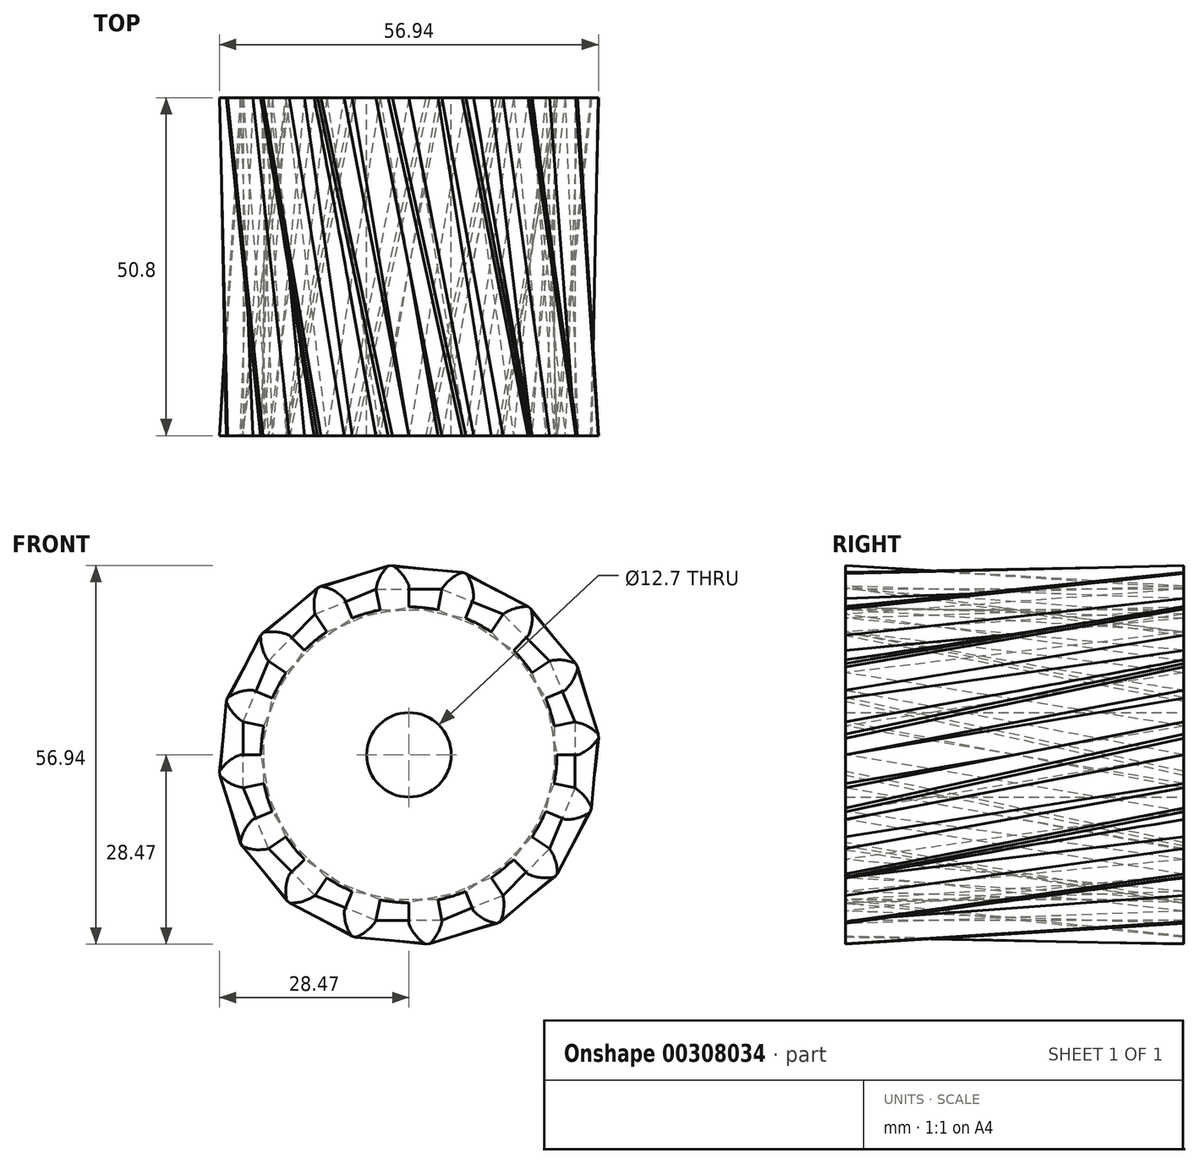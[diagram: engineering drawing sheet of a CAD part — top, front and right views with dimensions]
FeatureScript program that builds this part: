
annotation { "Feature Type Name" : "Feature", "Feature Type Description" : "" }
export const myFeature = defineFeature(function(context is Context, id is Id, definition is map)
    precondition{}
    {
        {
            var Q0;
            Q0=qCreatedBy(makeId("Front.planeOp"),FACE);
            var sketch = newSketch(context, id + "F0", { "sketchPlane" : qUnion([Q0])});
            skArc(sketch, "E0", {"start": v(-4.34, 21.8) * mm, "mid": v(-6.45, 21.27) * mm, "end": v(-8.5, 20.53) * mm});
            skArc(sketch, "E1.trimOffspring", {"start": v(0, 25.4) * mm, "mid": v(-1, 27.13) * mm, "end": v(-2.5, 28.47) * mm});
            skLineSegment(sketch, "E2", {"start": v(0, 25.4) * mm, "end": v(0, 22.23) * mm});
            skLineSegment(sketch, "E3", {"start": v(-2.5, 28.47) * mm, "end": v(-2.8, 28.44) * mm});
            skLineSegment(sketch, "E4.MirrorCS", {"start": v(-3.1, 28.4) * mm, "end": v(-2.8, 28.44) * mm});
            skArc(sketch, "E5.MirrorCS", {"start": v(-4.96, 24.91) * mm, "mid": v(-4.3, 26.8) * mm, "end": v(-3.1, 28.4) * mm});
            skLineSegment(sketch, "E6.MirrorCS", {"start": v(-4.96, 24.91) * mm, "end": v(-4.34, 21.8) * mm});
            skLineSegment(sketch, "E7.1.0", {"start": v(-14.11, 21.12) * mm, "end": v(-12.35, 18.48) * mm});
            skArc(sketch, "E7.1.1", {"start": v(-14.11, 21.12) * mm, "mid": v(-14.24, 23.12) * mm, "end": v(-13.74, 25.06) * mm});
            skLineSegment(sketch, "E7.1.2", {"start": v(-13.74, 25.06) * mm, "end": v(-13.47, 25.2) * mm});
            skLineSegment(sketch, "E7.1.3", {"start": v(-13.2, 25.34) * mm, "end": v(-13.47, 25.2) * mm});
            skArc(sketch, "E7.1.4", {"start": v(-9.72, 23.47) * mm, "mid": v(-11.31, 24.68) * mm, "end": v(-13.2, 25.34) * mm});
            skLineSegment(sketch, "E7.1.5", {"start": v(-9.72, 23.47) * mm, "end": v(-8.5, 20.53) * mm});
            skLineSegment(sketch, "E7.2.0", {"start": v(-21.12, 14.11) * mm, "end": v(-18.48, 12.35) * mm});
            skArc(sketch, "E7.2.1", {"start": v(-21.12, 14.11) * mm, "mid": v(-22, 15.9) * mm, "end": v(-22.28, 17.9) * mm});
            skLineSegment(sketch, "E7.2.2", {"start": v(-22.28, 17.9) * mm, "end": v(-22.09, 18.13) * mm});
            skLineSegment(sketch, "E7.2.3", {"start": v(-21.9, 18.36) * mm, "end": v(-22.09, 18.13) * mm});
            skArc(sketch, "E7.2.4", {"start": v(-17.96, 17.96) * mm, "mid": v(-19.9, 18.48) * mm, "end": v(-21.9, 18.36) * mm});
            skLineSegment(sketch, "E7.2.5", {"start": v(-17.96, 17.96) * mm, "end": v(-15.72, 15.72) * mm});
            skLineSegment(sketch, "E7.3.0", {"start": v(-24.91, 4.96) * mm, "end": v(-21.8, 4.34) * mm});
            skArc(sketch, "E7.3.1", {"start": v(-24.91, 4.96) * mm, "mid": v(-26.41, 6.28) * mm, "end": v(-27.43, 8) * mm});
            skLineSegment(sketch, "E7.3.2", {"start": v(-27.43, 8) * mm, "end": v(-27.34, 8.3) * mm});
            skLineSegment(sketch, "E7.3.3", {"start": v(-27.25, 8.59) * mm, "end": v(-27.34, 8.3) * mm});
            skArc(sketch, "E7.3.4", {"start": v(-23.47, 9.72) * mm, "mid": v(-25.45, 9.46) * mm, "end": v(-27.25, 8.59) * mm});
            skLineSegment(sketch, "E7.3.5", {"start": v(-23.47, 9.72) * mm, "end": v(-20.53, 8.5) * mm});
            skLineSegment(sketch, "E7.4.0", {"start": v(-24.91, -4.96) * mm, "end": v(-21.8, -4.34) * mm});
            skArc(sketch, "E7.4.1", {"start": v(-24.91, -4.96) * mm, "mid": v(-26.8, -4.3) * mm, "end": v(-28.4, -3.1) * mm});
            skLineSegment(sketch, "E7.4.2", {"start": v(-28.4, -3.1) * mm, "end": v(-28.44, -2.8) * mm});
            skLineSegment(sketch, "E7.4.3", {"start": v(-28.47, -2.5) * mm, "end": v(-28.44, -2.8) * mm});
            skArc(sketch, "E7.4.4", {"start": v(-25.4, 0) * mm, "mid": v(-27.13, -1) * mm, "end": v(-28.47, -2.5) * mm});
            skLineSegment(sketch, "E7.4.5", {"start": v(-25.4, 0) * mm, "end": v(-22.23, 0) * mm});
            skLineSegment(sketch, "E7.5.0", {"start": v(-21.12, -14.11) * mm, "end": v(-18.48, -12.35) * mm});
            skArc(sketch, "E7.5.1", {"start": v(-21.12, -14.11) * mm, "mid": v(-23.12, -14.24) * mm, "end": v(-25.06, -13.74) * mm});
            skLineSegment(sketch, "E7.5.2", {"start": v(-25.06, -13.74) * mm, "end": v(-25.2, -13.47) * mm});
            skLineSegment(sketch, "E7.5.3", {"start": v(-25.34, -13.2) * mm, "end": v(-25.2, -13.47) * mm});
            skArc(sketch, "E7.5.4", {"start": v(-23.47, -9.72) * mm, "mid": v(-24.68, -11.31) * mm, "end": v(-25.34, -13.2) * mm});
            skLineSegment(sketch, "E7.5.5", {"start": v(-23.47, -9.72) * mm, "end": v(-20.53, -8.5) * mm});
            skLineSegment(sketch, "E7.6.0", {"start": v(-14.11, -21.12) * mm, "end": v(-12.35, -18.48) * mm});
            skArc(sketch, "E7.6.1", {"start": v(-14.11, -21.12) * mm, "mid": v(-15.9, -22) * mm, "end": v(-17.9, -22.28) * mm});
            skLineSegment(sketch, "E7.6.2", {"start": v(-17.9, -22.28) * mm, "end": v(-18.13, -22.09) * mm});
            skLineSegment(sketch, "E7.6.3", {"start": v(-18.36, -21.9) * mm, "end": v(-18.13, -22.09) * mm});
            skArc(sketch, "E7.6.4", {"start": v(-17.96, -17.96) * mm, "mid": v(-18.48, -19.9) * mm, "end": v(-18.36, -21.9) * mm});
            skLineSegment(sketch, "E7.6.5", {"start": v(-17.96, -17.96) * mm, "end": v(-15.72, -15.72) * mm});
            skLineSegment(sketch, "E7.7.0", {"start": v(-4.96, -24.91) * mm, "end": v(-4.34, -21.8) * mm});
            skArc(sketch, "E7.7.1", {"start": v(-4.96, -24.91) * mm, "mid": v(-6.28, -26.41) * mm, "end": v(-8, -27.43) * mm});
            skLineSegment(sketch, "E7.7.2", {"start": v(-8, -27.43) * mm, "end": v(-8.3, -27.34) * mm});
            skLineSegment(sketch, "E7.7.3", {"start": v(-8.59, -27.25) * mm, "end": v(-8.3, -27.34) * mm});
            skArc(sketch, "E7.7.4", {"start": v(-9.72, -23.47) * mm, "mid": v(-9.46, -25.45) * mm, "end": v(-8.59, -27.25) * mm});
            skLineSegment(sketch, "E7.7.5", {"start": v(-9.72, -23.47) * mm, "end": v(-8.5, -20.53) * mm});
            skLineSegment(sketch, "E7.8.0", {"start": v(4.96, -24.91) * mm, "end": v(4.34, -21.8) * mm});
            skArc(sketch, "E7.8.1", {"start": v(4.96, -24.91) * mm, "mid": v(4.3, -26.8) * mm, "end": v(3.1, -28.4) * mm});
            skLineSegment(sketch, "E7.8.2", {"start": v(3.1, -28.4) * mm, "end": v(2.8, -28.44) * mm});
            skLineSegment(sketch, "E7.8.3", {"start": v(2.5, -28.47) * mm, "end": v(2.8, -28.44) * mm});
            skArc(sketch, "E7.8.4", {"start": v(0, -25.4) * mm, "mid": v(1, -27.13) * mm, "end": v(2.5, -28.47) * mm});
            skLineSegment(sketch, "E7.8.5", {"start": v(0, -25.4) * mm, "end": v(0, -22.23) * mm});
            skLineSegment(sketch, "E7.9.0", {"start": v(14.11, -21.12) * mm, "end": v(12.35, -18.48) * mm});
            skArc(sketch, "E7.9.1", {"start": v(14.11, -21.12) * mm, "mid": v(14.24, -23.12) * mm, "end": v(13.74, -25.06) * mm});
            skLineSegment(sketch, "E7.9.2", {"start": v(13.74, -25.06) * mm, "end": v(13.47, -25.2) * mm});
            skLineSegment(sketch, "E7.9.3", {"start": v(13.2, -25.34) * mm, "end": v(13.47, -25.2) * mm});
            skArc(sketch, "E7.9.4", {"start": v(9.72, -23.47) * mm, "mid": v(11.31, -24.68) * mm, "end": v(13.2, -25.34) * mm});
            skLineSegment(sketch, "E7.9.5", {"start": v(9.72, -23.47) * mm, "end": v(8.5, -20.53) * mm});
            skLineSegment(sketch, "E7.10.0", {"start": v(21.12, -14.11) * mm, "end": v(18.48, -12.35) * mm});
            skArc(sketch, "E7.10.1", {"start": v(21.12, -14.11) * mm, "mid": v(22, -15.9) * mm, "end": v(22.28, -17.9) * mm});
            skLineSegment(sketch, "E7.10.2", {"start": v(22.28, -17.9) * mm, "end": v(22.09, -18.13) * mm});
            skLineSegment(sketch, "E7.10.3", {"start": v(21.9, -18.36) * mm, "end": v(22.09, -18.13) * mm});
            skArc(sketch, "E7.10.4", {"start": v(17.96, -17.96) * mm, "mid": v(19.9, -18.48) * mm, "end": v(21.9, -18.36) * mm});
            skLineSegment(sketch, "E7.10.5", {"start": v(17.96, -17.96) * mm, "end": v(15.72, -15.72) * mm});
            skLineSegment(sketch, "E7.11.0", {"start": v(24.91, -4.96) * mm, "end": v(21.8, -4.34) * mm});
            skArc(sketch, "E7.11.1", {"start": v(24.91, -4.96) * mm, "mid": v(26.41, -6.28) * mm, "end": v(27.43, -8) * mm});
            skLineSegment(sketch, "E7.11.2", {"start": v(27.43, -8) * mm, "end": v(27.34, -8.3) * mm});
            skLineSegment(sketch, "E7.11.3", {"start": v(27.25, -8.59) * mm, "end": v(27.34, -8.3) * mm});
            skArc(sketch, "E7.11.4", {"start": v(23.47, -9.72) * mm, "mid": v(25.45, -9.46) * mm, "end": v(27.25, -8.59) * mm});
            skLineSegment(sketch, "E7.11.5", {"start": v(23.47, -9.72) * mm, "end": v(20.53, -8.5) * mm});
            skLineSegment(sketch, "E7.12.0", {"start": v(24.91, 4.96) * mm, "end": v(21.8, 4.34) * mm});
            skArc(sketch, "E7.12.1", {"start": v(24.91, 4.96) * mm, "mid": v(26.8, 4.3) * mm, "end": v(28.4, 3.1) * mm});
            skLineSegment(sketch, "E7.12.2", {"start": v(28.4, 3.1) * mm, "end": v(28.44, 2.8) * mm});
            skLineSegment(sketch, "E7.12.3", {"start": v(28.47, 2.5) * mm, "end": v(28.44, 2.8) * mm});
            skArc(sketch, "E7.12.4", {"start": v(25.4, 0) * mm, "mid": v(27.13, 1) * mm, "end": v(28.47, 2.5) * mm});
            skLineSegment(sketch, "E7.12.5", {"start": v(25.4, 0) * mm, "end": v(22.23, 0) * mm});
            skLineSegment(sketch, "E7.13.0", {"start": v(21.12, 14.11) * mm, "end": v(18.48, 12.35) * mm});
            skArc(sketch, "E7.13.1", {"start": v(21.12, 14.11) * mm, "mid": v(23.12, 14.24) * mm, "end": v(25.06, 13.74) * mm});
            skLineSegment(sketch, "E7.13.2", {"start": v(25.06, 13.74) * mm, "end": v(25.2, 13.47) * mm});
            skLineSegment(sketch, "E7.13.3", {"start": v(25.34, 13.2) * mm, "end": v(25.2, 13.47) * mm});
            skArc(sketch, "E7.13.4", {"start": v(23.47, 9.72) * mm, "mid": v(24.68, 11.31) * mm, "end": v(25.34, 13.2) * mm});
            skLineSegment(sketch, "E7.13.5", {"start": v(23.47, 9.72) * mm, "end": v(20.53, 8.5) * mm});
            skLineSegment(sketch, "E7.14.0", {"start": v(14.11, 21.12) * mm, "end": v(12.35, 18.48) * mm});
            skArc(sketch, "E7.14.1", {"start": v(14.11, 21.12) * mm, "mid": v(15.9, 22) * mm, "end": v(17.9, 22.28) * mm});
            skLineSegment(sketch, "E7.14.2", {"start": v(17.9, 22.28) * mm, "end": v(18.13, 22.09) * mm});
            skLineSegment(sketch, "E7.14.3", {"start": v(18.36, 21.9) * mm, "end": v(18.13, 22.09) * mm});
            skArc(sketch, "E7.14.4", {"start": v(17.96, 17.96) * mm, "mid": v(18.48, 19.9) * mm, "end": v(18.36, 21.9) * mm});
            skLineSegment(sketch, "E7.14.5", {"start": v(17.96, 17.96) * mm, "end": v(15.72, 15.72) * mm});
            skLineSegment(sketch, "E7.15.0", {"start": v(4.96, 24.91) * mm, "end": v(4.34, 21.8) * mm});
            skArc(sketch, "E7.15.1", {"start": v(4.96, 24.91) * mm, "mid": v(6.28, 26.41) * mm, "end": v(8, 27.43) * mm});
            skLineSegment(sketch, "E7.15.2", {"start": v(8, 27.43) * mm, "end": v(8.3, 27.34) * mm});
            skLineSegment(sketch, "E7.15.3", {"start": v(8.59, 27.25) * mm, "end": v(8.3, 27.34) * mm});
            skArc(sketch, "E7.15.4", {"start": v(9.72, 23.47) * mm, "mid": v(9.46, 25.45) * mm, "end": v(8.59, 27.25) * mm});
            skLineSegment(sketch, "E7.15.5", {"start": v(9.72, 23.47) * mm, "end": v(8.5, 20.53) * mm});
            skArc(sketch, "E8.trimOffspring", {"start": v(4.34, 21.8) * mm, "mid": v(2.18, 22.12) * mm, "end": v(0, 22.23) * mm});
            skArc(sketch, "E9.trimOffspring", {"start": v(-12.35, 18.48) * mm, "mid": v(-14.1, 17.18) * mm, "end": v(-15.72, 15.72) * mm});
            skArc(sketch, "E10.trimOffspring", {"start": v(12.35, 18.48) * mm, "mid": v(10.48, 19.6) * mm, "end": v(8.5, 20.53) * mm});
            skArc(sketch, "E11.trimOffspring", {"start": v(18.48, 12.35) * mm, "mid": v(17.18, 14.1) * mm, "end": v(15.72, 15.72) * mm});
            skArc(sketch, "E12.trimOffspring", {"start": v(21.8, 4.34) * mm, "mid": v(21.27, 6.45) * mm, "end": v(20.53, 8.5) * mm});
            skArc(sketch, "E13.trimOffspring", {"start": v(21.8, -4.34) * mm, "mid": v(22.12, -2.18) * mm, "end": v(22.23, 0) * mm});
            skArc(sketch, "E14.trimOffspring", {"start": v(18.48, -12.35) * mm, "mid": v(19.6, -10.48) * mm, "end": v(20.53, -8.5) * mm});
            skArc(sketch, "E15.trimOffspring", {"start": v(12.35, -18.48) * mm, "mid": v(14.1, -17.18) * mm, "end": v(15.72, -15.72) * mm});
            skArc(sketch, "E16.trimOffspring", {"start": v(4.34, -21.8) * mm, "mid": v(6.45, -21.27) * mm, "end": v(8.5, -20.53) * mm});
            skArc(sketch, "E17.trimOffspring", {"start": v(-4.34, -21.8) * mm, "mid": v(-2.18, -22.12) * mm, "end": v(0, -22.23) * mm});
            skArc(sketch, "E18.trimOffspring", {"start": v(-12.35, -18.48) * mm, "mid": v(-10.48, -19.6) * mm, "end": v(-8.5, -20.53) * mm});
            skArc(sketch, "E19.trimOffspring", {"start": v(-18.48, -12.35) * mm, "mid": v(-17.18, -14.1) * mm, "end": v(-15.72, -15.72) * mm});
            skArc(sketch, "E20.trimOffspring", {"start": v(-21.8, -4.34) * mm, "mid": v(-21.27, -6.45) * mm, "end": v(-20.53, -8.5) * mm});
            skArc(sketch, "E21.trimOffspring", {"start": v(-21.8, 4.34) * mm, "mid": v(-22.12, 2.18) * mm, "end": v(-22.23, 0) * mm});
            skArc(sketch, "E22.trimOffspring", {"start": v(-18.48, 12.35) * mm, "mid": v(-19.6, 10.48) * mm, "end": v(-20.53, 8.5) * mm});
            skSolve(sketch);
        }
        {
            var Q0;
            Q0=makeQuery(id+"F0.imprint","IMPRINT",FACE,{"disambiguationData":[TD([[makeQuery(id+"F0.imprint","IMPRINT",EDGE,{"derivedFrom":sQuery(id+"F0.wireOp",EDGE,"E0")}),1.0]])]});
            cPlane(context, id + "F1", {"entities" : qUnion([Q0]), "cplaneType" : CPlaneType.OFFSET, "offset" : 50.8 * mm, "width" : 152.4 * mm, "height" : 152.4 * mm});
        }
        {
            var Q0;
            Q0=qCreatedBy(id+"F1.planeOp",FACE);
            var sketch = newSketch(context, id + "F2", { "sketchPlane" : qUnion([Q0])});
            skArc(sketch, "E23.0.0", {"start": v(-27.43, 8) * mm, "mid": v(-26.41, 6.28) * mm, "end": v(-24.91, 4.96) * mm});
            skLineSegment(sketch, "E23.0.1", {"start": v(-24.91, 4.96) * mm, "end": v(-21.8, 4.34) * mm});
            skArc(sketch, "E23.0.2", {"start": v(-21.8, 4.34) * mm, "mid": v(-22.12, 2.18) * mm, "end": v(-22.23, 0) * mm});
            skLineSegment(sketch, "E23.0.3", {"start": v(-22.23, 0) * mm, "end": v(-25.4, 0) * mm});
            skArc(sketch, "E23.0.4", {"start": v(-25.4, 0) * mm, "mid": v(-27.13, -1) * mm, "end": v(-28.47, -2.5) * mm});
            skLineSegment(sketch, "E23.0.5", {"start": v(-28.47, -2.5) * mm, "end": v(-28.44, -2.8) * mm});
            skLineSegment(sketch, "E23.0.6", {"start": v(-28.44, -2.8) * mm, "end": v(-28.4, -3.1) * mm});
            skArc(sketch, "E23.0.7", {"start": v(-28.4, -3.1) * mm, "mid": v(-26.8, -4.3) * mm, "end": v(-24.91, -4.96) * mm});
            skLineSegment(sketch, "E23.0.8", {"start": v(-24.91, -4.96) * mm, "end": v(-21.8, -4.34) * mm});
            skArc(sketch, "E23.0.9", {"start": v(-21.8, -4.34) * mm, "mid": v(-21.27, -6.45) * mm, "end": v(-20.53, -8.5) * mm});
            skLineSegment(sketch, "E23.0.10", {"start": v(-20.53, -8.5) * mm, "end": v(-23.47, -9.72) * mm});
            skArc(sketch, "E23.0.11", {"start": v(-23.47, -9.72) * mm, "mid": v(-24.68, -11.31) * mm, "end": v(-25.34, -13.2) * mm});
            skLineSegment(sketch, "E23.0.12", {"start": v(-25.34, -13.2) * mm, "end": v(-25.2, -13.47) * mm});
            skLineSegment(sketch, "E23.0.13", {"start": v(-25.2, -13.47) * mm, "end": v(-25.06, -13.74) * mm});
            skArc(sketch, "E23.0.14", {"start": v(-25.06, -13.74) * mm, "mid": v(-23.12, -14.24) * mm, "end": v(-21.12, -14.11) * mm});
            skLineSegment(sketch, "E23.0.15", {"start": v(-21.12, -14.11) * mm, "end": v(-18.48, -12.35) * mm});
            skArc(sketch, "E23.0.16", {"start": v(-18.48, -12.35) * mm, "mid": v(-17.18, -14.1) * mm, "end": v(-15.72, -15.72) * mm});
            skLineSegment(sketch, "E23.0.17", {"start": v(-15.72, -15.72) * mm, "end": v(-17.96, -17.96) * mm});
            skArc(sketch, "E23.0.18", {"start": v(-17.96, -17.96) * mm, "mid": v(-18.48, -19.9) * mm, "end": v(-18.36, -21.9) * mm});
            skLineSegment(sketch, "E23.0.19", {"start": v(-18.36, -21.9) * mm, "end": v(-18.13, -22.09) * mm});
            skLineSegment(sketch, "E23.0.20", {"start": v(-18.13, -22.09) * mm, "end": v(-17.9, -22.28) * mm});
            skArc(sketch, "E23.0.21", {"start": v(-17.9, -22.28) * mm, "mid": v(-15.9, -22) * mm, "end": v(-14.11, -21.12) * mm});
            skLineSegment(sketch, "E23.0.22", {"start": v(-14.11, -21.12) * mm, "end": v(-12.35, -18.48) * mm});
            skArc(sketch, "E23.0.23", {"start": v(-12.35, -18.48) * mm, "mid": v(-10.48, -19.6) * mm, "end": v(-8.5, -20.53) * mm});
            skLineSegment(sketch, "E23.0.24", {"start": v(-8.5, -20.53) * mm, "end": v(-9.72, -23.47) * mm});
            skArc(sketch, "E23.0.25", {"start": v(-9.72, -23.47) * mm, "mid": v(-9.46, -25.45) * mm, "end": v(-8.59, -27.25) * mm});
            skLineSegment(sketch, "E23.0.26", {"start": v(-8.59, -27.25) * mm, "end": v(-8.3, -27.34) * mm});
            skLineSegment(sketch, "E23.0.27", {"start": v(-8.3, -27.34) * mm, "end": v(-8, -27.43) * mm});
            skArc(sketch, "E23.0.28", {"start": v(-8, -27.43) * mm, "mid": v(-6.28, -26.41) * mm, "end": v(-4.96, -24.91) * mm});
            skLineSegment(sketch, "E23.0.29", {"start": v(-4.96, -24.91) * mm, "end": v(-4.34, -21.8) * mm});
            skArc(sketch, "E23.0.30", {"start": v(-4.34, -21.8) * mm, "mid": v(-2.18, -22.12) * mm, "end": v(0, -22.23) * mm});
            skLineSegment(sketch, "E23.0.31", {"start": v(0, -22.23) * mm, "end": v(0, -25.4) * mm});
            skArc(sketch, "E23.0.32", {"start": v(0, -25.4) * mm, "mid": v(1, -27.13) * mm, "end": v(2.5, -28.47) * mm});
            skLineSegment(sketch, "E23.0.33", {"start": v(2.5, -28.47) * mm, "end": v(2.8, -28.44) * mm});
            skLineSegment(sketch, "E23.0.34", {"start": v(2.8, -28.44) * mm, "end": v(3.1, -28.4) * mm});
            skArc(sketch, "E23.0.35", {"start": v(3.1, -28.4) * mm, "mid": v(4.3, -26.8) * mm, "end": v(4.96, -24.91) * mm});
            skLineSegment(sketch, "E23.0.36", {"start": v(4.96, -24.91) * mm, "end": v(4.34, -21.8) * mm});
            skArc(sketch, "E23.0.37", {"start": v(4.34, -21.8) * mm, "mid": v(6.45, -21.27) * mm, "end": v(8.5, -20.53) * mm});
            skLineSegment(sketch, "E23.0.38", {"start": v(8.5, -20.53) * mm, "end": v(9.72, -23.47) * mm});
            skArc(sketch, "E23.0.39", {"start": v(9.72, -23.47) * mm, "mid": v(11.31, -24.68) * mm, "end": v(13.2, -25.34) * mm});
            skLineSegment(sketch, "E23.0.40", {"start": v(13.2, -25.34) * mm, "end": v(13.47, -25.2) * mm});
            skLineSegment(sketch, "E23.0.41", {"start": v(13.47, -25.2) * mm, "end": v(13.74, -25.06) * mm});
            skArc(sketch, "E23.0.42", {"start": v(13.74, -25.06) * mm, "mid": v(14.24, -23.12) * mm, "end": v(14.11, -21.12) * mm});
            skLineSegment(sketch, "E23.0.43", {"start": v(14.11, -21.12) * mm, "end": v(12.35, -18.48) * mm});
            skArc(sketch, "E23.0.44", {"start": v(12.35, -18.48) * mm, "mid": v(14.1, -17.18) * mm, "end": v(15.72, -15.72) * mm});
            skLineSegment(sketch, "E23.0.45", {"start": v(15.72, -15.72) * mm, "end": v(17.96, -17.96) * mm});
            skArc(sketch, "E23.0.46", {"start": v(17.96, -17.96) * mm, "mid": v(19.9, -18.48) * mm, "end": v(21.9, -18.36) * mm});
            skLineSegment(sketch, "E23.0.47", {"start": v(21.9, -18.36) * mm, "end": v(22.09, -18.13) * mm});
            skLineSegment(sketch, "E23.0.48", {"start": v(22.09, -18.13) * mm, "end": v(22.28, -17.9) * mm});
            skArc(sketch, "E23.0.49", {"start": v(22.28, -17.9) * mm, "mid": v(22, -15.9) * mm, "end": v(21.12, -14.11) * mm});
            skLineSegment(sketch, "E23.0.50", {"start": v(21.12, -14.11) * mm, "end": v(18.48, -12.35) * mm});
            skArc(sketch, "E23.0.51", {"start": v(18.48, -12.35) * mm, "mid": v(19.6, -10.48) * mm, "end": v(20.53, -8.5) * mm});
            skLineSegment(sketch, "E23.0.52", {"start": v(20.53, -8.5) * mm, "end": v(23.47, -9.72) * mm});
            skArc(sketch, "E23.0.53", {"start": v(23.47, -9.72) * mm, "mid": v(25.45, -9.46) * mm, "end": v(27.25, -8.59) * mm});
            skLineSegment(sketch, "E23.0.54", {"start": v(27.25, -8.59) * mm, "end": v(27.34, -8.3) * mm});
            skLineSegment(sketch, "E23.0.55", {"start": v(27.34, -8.3) * mm, "end": v(27.43, -8) * mm});
            skArc(sketch, "E23.0.56", {"start": v(27.43, -8) * mm, "mid": v(26.41, -6.28) * mm, "end": v(24.91, -4.96) * mm});
            skLineSegment(sketch, "E23.0.57", {"start": v(24.91, -4.96) * mm, "end": v(21.8, -4.34) * mm});
            skArc(sketch, "E23.0.58", {"start": v(21.8, -4.34) * mm, "mid": v(22.12, -2.18) * mm, "end": v(22.23, 0) * mm});
            skLineSegment(sketch, "E23.0.59", {"start": v(22.23, 0) * mm, "end": v(25.4, 0) * mm});
            skArc(sketch, "E23.0.60", {"start": v(25.4, 0) * mm, "mid": v(27.13, 1) * mm, "end": v(28.47, 2.5) * mm});
            skLineSegment(sketch, "E23.0.61", {"start": v(28.47, 2.5) * mm, "end": v(28.44, 2.8) * mm});
            skLineSegment(sketch, "E23.0.62", {"start": v(28.44, 2.8) * mm, "end": v(28.4, 3.1) * mm});
            skArc(sketch, "E23.0.63", {"start": v(28.4, 3.1) * mm, "mid": v(26.8, 4.3) * mm, "end": v(24.91, 4.96) * mm});
            skLineSegment(sketch, "E23.0.64", {"start": v(24.91, 4.96) * mm, "end": v(21.8, 4.34) * mm});
            skArc(sketch, "E23.0.65", {"start": v(21.8, 4.34) * mm, "mid": v(21.27, 6.45) * mm, "end": v(20.53, 8.5) * mm});
            skLineSegment(sketch, "E23.0.66", {"start": v(20.53, 8.5) * mm, "end": v(23.47, 9.72) * mm});
            skArc(sketch, "E23.0.67", {"start": v(23.47, 9.72) * mm, "mid": v(24.68, 11.31) * mm, "end": v(25.34, 13.2) * mm});
            skLineSegment(sketch, "E23.0.68", {"start": v(25.34, 13.2) * mm, "end": v(25.2, 13.47) * mm});
            skLineSegment(sketch, "E23.0.69", {"start": v(25.2, 13.47) * mm, "end": v(25.06, 13.74) * mm});
            skArc(sketch, "E23.0.70", {"start": v(25.06, 13.74) * mm, "mid": v(23.12, 14.24) * mm, "end": v(21.12, 14.11) * mm});
            skLineSegment(sketch, "E23.0.71", {"start": v(21.12, 14.11) * mm, "end": v(18.48, 12.35) * mm});
            skArc(sketch, "E23.0.72", {"start": v(18.48, 12.35) * mm, "mid": v(17.18, 14.1) * mm, "end": v(15.72, 15.72) * mm});
            skLineSegment(sketch, "E23.0.73", {"start": v(15.72, 15.72) * mm, "end": v(17.96, 17.96) * mm});
            skArc(sketch, "E23.0.74", {"start": v(17.96, 17.96) * mm, "mid": v(18.48, 19.9) * mm, "end": v(18.36, 21.9) * mm});
            skLineSegment(sketch, "E23.0.75", {"start": v(18.36, 21.9) * mm, "end": v(18.13, 22.09) * mm});
            skLineSegment(sketch, "E23.0.76", {"start": v(18.13, 22.09) * mm, "end": v(17.9, 22.28) * mm});
            skArc(sketch, "E23.0.77", {"start": v(17.9, 22.28) * mm, "mid": v(15.9, 22) * mm, "end": v(14.11, 21.12) * mm});
            skLineSegment(sketch, "E23.0.78", {"start": v(14.11, 21.12) * mm, "end": v(12.35, 18.48) * mm});
            skArc(sketch, "E23.0.79", {"start": v(12.35, 18.48) * mm, "mid": v(10.48, 19.6) * mm, "end": v(8.5, 20.53) * mm});
            skLineSegment(sketch, "E23.0.80", {"start": v(8.5, 20.53) * mm, "end": v(9.72, 23.47) * mm});
            skArc(sketch, "E23.0.81", {"start": v(9.72, 23.47) * mm, "mid": v(9.46, 25.45) * mm, "end": v(8.59, 27.25) * mm});
            skLineSegment(sketch, "E23.0.82", {"start": v(8.59, 27.25) * mm, "end": v(8.3, 27.34) * mm});
            skLineSegment(sketch, "E23.0.83", {"start": v(8.3, 27.34) * mm, "end": v(8, 27.43) * mm});
            skArc(sketch, "E23.0.84", {"start": v(8, 27.43) * mm, "mid": v(6.28, 26.41) * mm, "end": v(4.96, 24.91) * mm});
            skLineSegment(sketch, "E23.0.85", {"start": v(4.96, 24.91) * mm, "end": v(4.34, 21.8) * mm});
            skArc(sketch, "E23.0.86", {"start": v(4.34, 21.8) * mm, "mid": v(2.18, 22.12) * mm, "end": v(0, 22.23) * mm});
            skLineSegment(sketch, "E23.0.87", {"start": v(0, 22.23) * mm, "end": v(0, 25.4) * mm});
            skArc(sketch, "E23.0.88", {"start": v(0, 25.4) * mm, "mid": v(-1, 27.13) * mm, "end": v(-2.5, 28.47) * mm});
            skLineSegment(sketch, "E23.0.89", {"start": v(-2.5, 28.47) * mm, "end": v(-2.8, 28.44) * mm});
            skLineSegment(sketch, "E23.0.90", {"start": v(-2.8, 28.44) * mm, "end": v(-3.1, 28.4) * mm});
            skArc(sketch, "E23.0.91", {"start": v(-3.1, 28.4) * mm, "mid": v(-4.3, 26.8) * mm, "end": v(-4.96, 24.91) * mm});
            skLineSegment(sketch, "E23.0.92", {"start": v(-4.96, 24.91) * mm, "end": v(-4.34, 21.8) * mm});
            skArc(sketch, "E23.0.93", {"start": v(-4.34, 21.8) * mm, "mid": v(-6.45, 21.27) * mm, "end": v(-8.5, 20.53) * mm});
            skLineSegment(sketch, "E23.0.94", {"start": v(-8.5, 20.53) * mm, "end": v(-9.72, 23.47) * mm});
            skArc(sketch, "E23.0.95", {"start": v(-9.72, 23.47) * mm, "mid": v(-11.31, 24.68) * mm, "end": v(-13.2, 25.34) * mm});
            skLineSegment(sketch, "E23.0.96", {"start": v(-13.2, 25.34) * mm, "end": v(-13.47, 25.2) * mm});
            skLineSegment(sketch, "E23.0.97", {"start": v(-13.47, 25.2) * mm, "end": v(-13.74, 25.06) * mm});
            skArc(sketch, "E23.0.98", {"start": v(-13.74, 25.06) * mm, "mid": v(-14.24, 23.12) * mm, "end": v(-14.11, 21.12) * mm});
            skLineSegment(sketch, "E23.0.99", {"start": v(-14.11, 21.12) * mm, "end": v(-12.35, 18.48) * mm});
            skArc(sketch, "E23.0.100", {"start": v(-12.35, 18.48) * mm, "mid": v(-14.1, 17.18) * mm, "end": v(-15.72, 15.72) * mm});
            skLineSegment(sketch, "E23.0.101", {"start": v(-15.72, 15.72) * mm, "end": v(-17.96, 17.96) * mm});
            skArc(sketch, "E23.0.102", {"start": v(-17.96, 17.96) * mm, "mid": v(-19.9, 18.48) * mm, "end": v(-21.9, 18.36) * mm});
            skLineSegment(sketch, "E23.0.103", {"start": v(-21.9, 18.36) * mm, "end": v(-22.09, 18.13) * mm});
            skLineSegment(sketch, "E23.0.104", {"start": v(-22.09, 18.13) * mm, "end": v(-22.28, 17.9) * mm});
            skArc(sketch, "E23.0.105", {"start": v(-22.28, 17.9) * mm, "mid": v(-22, 15.9) * mm, "end": v(-21.12, 14.11) * mm});
            skLineSegment(sketch, "E23.0.106", {"start": v(-21.12, 14.11) * mm, "end": v(-18.48, 12.35) * mm});
            skArc(sketch, "E23.0.107", {"start": v(-18.48, 12.35) * mm, "mid": v(-19.6, 10.48) * mm, "end": v(-20.53, 8.5) * mm});
            skLineSegment(sketch, "E23.0.108", {"start": v(-20.53, 8.5) * mm, "end": v(-23.47, 9.72) * mm});
            skArc(sketch, "E23.0.109", {"start": v(-23.47, 9.72) * mm, "mid": v(-25.45, 9.46) * mm, "end": v(-27.25, 8.59) * mm});
            skLineSegment(sketch, "E23.0.110", {"start": v(-27.25, 8.59) * mm, "end": v(-27.34, 8.3) * mm});
            skLineSegment(sketch, "E23.0.111", {"start": v(-27.34, 8.3) * mm, "end": v(-27.43, 8) * mm});
            skSolve(sketch);
        }
        {
            var Q0;
            Q0=makeQuery(id+"F0.imprint","IMPRINT",FACE,{"disambiguationData":[TD([[makeQuery(id+"F0.imprint","IMPRINT",EDGE,{"derivedFrom":sQuery(id+"F0.wireOp",EDGE,"E0")}),1.0]])]});
            var Q1;
            Q1=makeQuery(id+"F2.imprint","IMPRINT",FACE,{"disambiguationData":[TD([[makeQuery(id+"F2.imprint","IMPRINT",EDGE,{"derivedFrom":sQuery(id+"F2.wireOp",EDGE,"E23.0.0")}),1.0]])]});
            var Q2;
            Q2=sQuery(id+"F2.wireOp",VERTEX,"E23.0.93.start");
            var Q3;
            Q3=sQuery(id+"F0.wireOp",VERTEX,"E7.1.0.end");
            loft(context, id + "F3", {"sheetProfilesArray" : [{ "sheetProfileEntities" : qUnion([Q0]) }, { "sheetProfileEntities" : qUnion([Q1]) }], "matchConnections" : true, "connections" : [{ "connectionEntities" : qUnion([Q2, Q3]), "connectionEdgeQueries" : qUnion([]), "connectionEdgeParameters" : [] }]});
        }
        {
            var Q0;
            Q0=makeQuery(id+"F3.opLoft","CAP_FACE",FACE,{"disambiguationData":[OSD([makeQuery(id+"F0.imprint","IMPRINT",FACE,{"disambiguationData":[TD([[makeQuery(id+"F0.imprint","IMPRINT",EDGE,{"derivedFrom":sQuery(id+"F0.wireOp",EDGE,"E0")}),1.0]])]})])],"isStart":true});
            var sketch = newSketch(context, id + "F4", { "sketchPlane" : qUnion([Q0])});
            skCircle(sketch, "E24", {"center": v(0, 0) * mm, "radius": 6.35 * mm});
            skSolve(sketch);
        }
        {
            var Q0;
            Q0=makeQuery(id+"F4.imprint","IMPRINT",FACE,{"disambiguationData":[TD([[makeQuery(id+"F4.imprint","IMPRINT",EDGE,{"derivedFrom":sQuery(id+"F4.wireOp",EDGE,"E24")}),1.0]])]});
            extrude(context, id + "F5", {"entities" : qUnion([Q0]), "operationType" : NewBodyOperationType.REMOVE, "endBound" : BoundingType.THROUGH_ALL, "oppositeDirection" : true, "depth" : 25.4 * mm});
        }
    });
